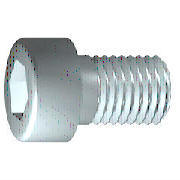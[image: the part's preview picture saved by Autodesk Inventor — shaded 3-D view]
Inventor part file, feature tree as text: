
AUTODESK INVENTOR PART (.ipt)
format: ipt  version: 2022 (Build 260153000, 153)  size: 193,024 bytes
history: native  units: mm (DEFAULTED — no unit token found)
features: sketch x2, other x1, extrude x1, plane x1, fillet x1
ambient origin geometry x7: Origin, YZ Plane, XY Plane, X Axis, Y Axis, Z Axis, Center Point
bodies: Solid1 (feature_tree)
feature tree (6):
  other  "Körper"
  extrude  "Loch"  Depth=3.0mm
  plane  "Work Plane1"
  fillet  "Fillet2"  Radius=3.0mm
  sketch  "Skizze1"  dims[d1=14.75mm d2=0.306825mm d3=3.0mm]
  sketch  "Skizze2"  dims[d4=1.3mm d5=60.0deg d6=3.0mm d7=3.0mm d8=2.886751mm d9=5.5mm d10=90.0deg d11=10.0mm d12=0.0mm d13=14.75mm d14=0.0mm d15=0.306725mm d16=0.306725mm d17=0.3mm d19=0.0mm d26=16.0mm d27=45.0deg d28=0.0mm d29=0.0mm d30=0.1mm]
